AUTODESK INVENTOR PART (.ipt)
format: ipt  version: 2024 (Build 280153000, 153)  size: 107,520 bytes
history: native  units: mm
features: other x3, plane x1, sketch x1
ambient origin geometry x8: Origin, YZ Plane, XZ Plane, XY Plane, X Axis, Y Axis, Z Axis, Center Point
feature tree (5):
  plane  "Plano de trabajo1"
  sketch  "Boceto1"
  other  "<userpath>\Downloads\Celda_Robotizada.iam"
  other  "Celda_Robotizada.iam"
  other  "Mesa:1"
